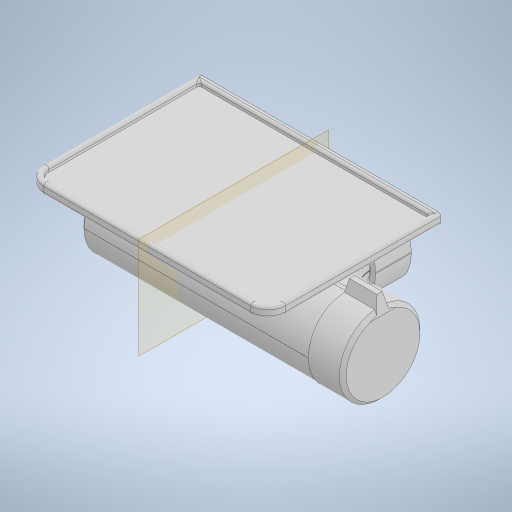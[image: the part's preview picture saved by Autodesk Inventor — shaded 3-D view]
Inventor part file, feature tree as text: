
AUTODESK INVENTOR PART (.ipt)
format: ipt  version: 2024.1 (Build 281209000, 209)  size: 555,008 bytes
history: native  units: mm
features: fillet x11, extrude x7, sketch x7, chamfer x4, projected_geometry x4, plane x1, other x1
ambient origin geometry x8: Origin, YZ Plane, XZ Plane, XY Plane, X Axis, Y Axis, Z Axis, Center Point
bodies: Solid1 (feature_tree)
feature tree (35):
  extrude  "Extrusion1"  Depth=36.0mm
  fillet  "Fillet1"  Radius=46.7mm
  fillet  "Fillet2"  Radius=26.0mm
  fillet  "Fillet3"  Radius=26.0mm
  extrude  "Extrusion2"  Depth=44.56mm TaperAngle=0.0deg
  extrude  "Extrusion3"  Depth=22.25mm
  chamfer  "Chamfer1"  Distance=20.0mm
  chamfer  "Chamfer2"  Distance=30.0mm
  chamfer  "Chamfer3"  Distance=3.0mm
  chamfer  "Chamfer4"  Distance=3.0mm
  extrude  "Extrusion4"  Depth=1.5mm
  extrude  "Extrusion5"  Depth=20.0mm TaperAngle=0.0deg
  fillet  "Fillet4"  Radius=2.0mm
  fillet  "Fillet5"  Radius=10.0mm
  extrude  "Extrusion6"  Depth=10.0mm TaperAngle=45.0deg
  fillet  "Fillet6"  Radius=2.0mm
  fillet  "Fillet7"  Radius=60.0mm
  fillet  "Fillet8"  Radius=80.0mm
  fillet  "Fillet9"  Radius=100.0mm
  plane  "Work Plane1"
  extrude  "Extrusion7"  Depth=5.0mm TaperAngle=0.0deg
  fillet  "Fillet10"  Radius=3.0mm
  fillet  "Fillet11"  Radius=35.0mm
  sketch  "Sketch1"  dims[d0=80.0mm d1=36.0mm d2=46.7mm d3=26.0mm d4=26.0mm]
  sketch  "Sketch2"  dims[d5=132.0mm d6=44.56mm d7=0.0mm]
  sketch  "Sketch3"  dims[d8=22.0mm d9=22.25mm]
  sketch  "Sketch4"  dims[d10=15.0mm]
  other  "TRAY"
  sketch  "Sketch5"  dims[d11=46.7mm]
  projected_geometry  "Projected Loop1"
  sketch  "Sketch6"  dims[d12=44.56mm]
  projected_geometry  "Projected Loop2"
  sketch  "Sketch7"  dims[d13=22.28mm d14=20.0mm d15=0.0mm d16=30.0mm d17=3.0mm d18=3.0mm d19=1.5mm d20=20.0mm d21=0.0mm d22=2.0mm d23=2.0mm d24=45.0deg d25=10.0mm d26=2.0mm d27=45.0deg d28=10.0mm d29=2.0mm d30=45.0deg d31=2.0mm d32=2.0mm d33=45.0deg d34=60.0mm d35=80.0mm d36=100.0mm d37=3.0mm d38=0.0mm d39=3.0mm d40=35.0mm d41=20.75mm d42=0.0mm d43=5.0mm d44=10.0mm d45=3.0mm d46=3.0mm d47=0.0mm d48=1.5mm d49=1.5mm d50=1.5mm d51=1.5mm d52=3.0mm d54=18.0mm d55=100.0mm d56=0.0mm d57=5.0mm d58=5.0mm]
  projected_geometry  "Projected Loop3"
  projected_geometry  "Projected Loop4"
